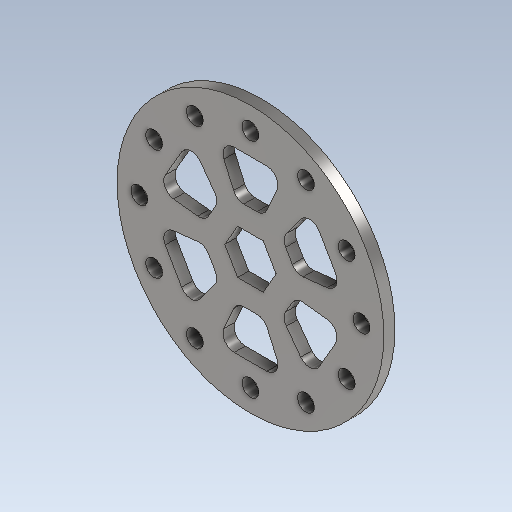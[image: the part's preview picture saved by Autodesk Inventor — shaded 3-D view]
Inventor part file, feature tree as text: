
AUTODESK INVENTOR PART (.ipt)
format: ipt  version: 2023 (Build 270158000, 158)  size: 228,864 bytes
history: native  units: in
note: dims shown in document units (in); Inventor stores cm internally (conversion verified against a paired STEP export)
features: other x3, sketch x1
ambient origin geometry x8: Origin, YZ Plane, XZ Plane, XY Plane, X Axis, Y Axis, Z Axis, Center Point
bodies: Solid1 (feature_tree)
feature tree (4):
  other  "ThickWheelPlate_v8.ipt"
  other  "Solid1::ThickWheelPlate_v8.ipt"
  other  "TaggingFeature1"
  sketch  "Sketch1"  dims[d0=0.3937in]
